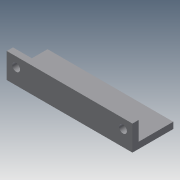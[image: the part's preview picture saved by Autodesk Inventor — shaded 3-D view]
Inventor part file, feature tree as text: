
AUTODESK INVENTOR PART (.ipt)
format: ipt  version: 2013 (Build 170138000, 138)  size: 99,328 bytes
history: native  units: mm
features: sketch x5, extrude x4
ambient origin geometry x8: Origin, YZ Plane, XZ Plane, XY Plane, X Axis, Y Axis, Z Axis, Center Point
bodies: Solid1 (feature_tree)
feature tree (9):
  sketch  "Sketch1"  dims[d0=40.0mm d1=6.0mm]
  sketch  "Sketch2"  dims[d2=2.0mm d3=0.0mm d4=2.0mm]
  extrude  "Extrusion1"  Depth=6.0mm
  extrude  "Extrusion2"  Depth=2.0mm
  extrude  "Extrusion3"  Depth=2.0mm TaperAngle=0.0deg
  extrude  "Extrusion4"  Depth=2.5mm
  sketch  "Sketch3"  dims[d5=11.0mm d6=0.0mm d7=2.0mm d8=0.0mm]
  sketch  "Sketch4"  dims[d9=3.0mm d10=2.5mm]
  sketch  "Sketch5"  dims[d11=3.0mm d12=3.0mm d13=2.5mm d14=2.0mm d15=0.0mm]
